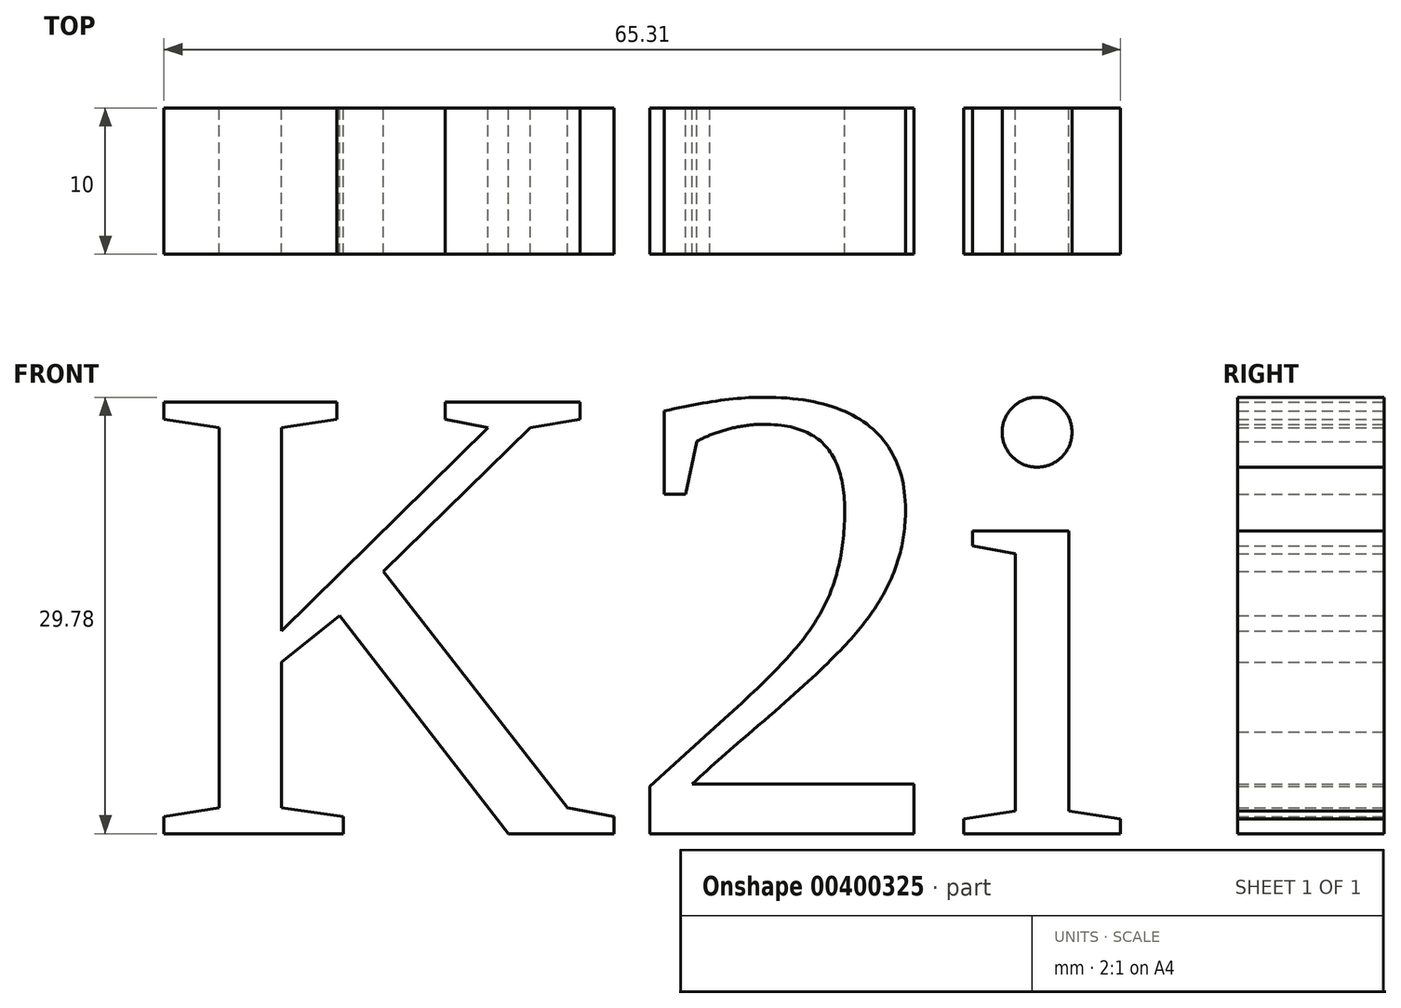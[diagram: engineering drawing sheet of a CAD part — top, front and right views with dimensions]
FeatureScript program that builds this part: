
annotation { "Feature Type Name" : "Feature", "Feature Type Description" : "" }
export const myFeature = defineFeature(function(context is Context, id is Id, definition is map)
    precondition{}
    {
        {
            var Q0;
            Q0=qCreatedBy(makeId("Front.planeOp"),FACE);
            var sketch = newSketch(context, id + "F0", { "sketchPlane" : qUnion([Q0])});
            skText(sketch, "E0", { "text": "K2i", "fontName": "Tinos-Regular.ttf"});
            const initialGuessF0  = {"E0": [0, 0, 1, 0, 0.03238]};
            skSetInitialGuess(sketch, initialGuessF0);
            skSolve(sketch);
        }
        {
            var Q0;
            Q0 = qSketchRegion(id + "F0", true);
            extrude(context, id + "F1", {"entities" : qUnion([Q0]), "depth" : 10 * mm});
        }
    });
